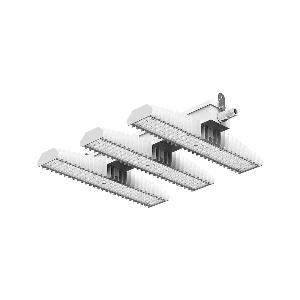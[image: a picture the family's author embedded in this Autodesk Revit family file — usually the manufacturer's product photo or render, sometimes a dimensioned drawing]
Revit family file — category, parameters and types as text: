
# Revit family: 3f_filippi_-_3f_lem_ho_ampio_3f_filippi_-_58973_-_3f_lem_3_ho_led_210_dali_cr_ampio
name_source: partatom
category: Lighting Fixtures
units: mm (PartAtom-declared; Revit-internal decimal feet)

## family parameters
Cut with Voids When Loaded = No
Host = Face
Light Source = No
Part Type = Normal
Room Calculation Point = No
Round Connector Dimension = Use Diameter
Shared = No

## types (1)
- 3F Filippi - 3F LEM HO Ampio (1 x LED, 33909 lm, 207 W, 4000 K)
    Apparent Load = 207 VA
    Approval mark = CE
    CIE Flux Codes = 60 92 99 100 100
    Color Rendering = 80
    Color Temperature = 4000 K
    Control Gear = Electronic transformer
    Default Elevation = 1800 mm
    Description = Industrial luminaire with high light output and high luminous efficiency designed with the most innovative technologies for environments with temperature up to 55°C.

ILLUMINOTECHNICAL
Luminous efficiency 100% (DLOR 100%, ULOR 0%).
Initial luminous flux of the luminaire 33909 lm.
Direct symmetric wide distribution: the illuminated area has a rectangular shape.
Installation Interdistance Transv.D = 1.58 x hu - Long.D = 1.45 x hu.
Tabular UGR (CIE 117 - 4H-8H; S=0.25H; 70/50/20): RUG 24.2 - 25.2.
Beam angle: 93° - 99°.
Luminous efficacy 164 lm/W.
Lifetime (L93/B10): 30000 h. (tq+25°C)
Lifetime (L90/B10): 50000 h. (tq+25°C)
Lifetime (L85/B10): 80000 h. (tq+25°C)
Lifetime (L80/B10): 100000 h. (tq+25°C)
Lifetime (L85/B10): 50000 h. (tq+55°C)
Sudden decreased luminous flux after 50000 hours: 0% (C0).
Photobiological safety in compliance with IEC/TR 62778: RG0 risk exempt, (IEC 62471).
In compliance with IEC/EN 62722-2-1 - IEC/EN 62717 standards.

SOURCE
3 Mid-Power linear LED modules 70W/840.
Energy efficiency class (UE 2019/2020 - UE 2019/2015): C.
CIE 13.3 Colour rendering index: CRI >80 (R9 <50%).
IES TM-30 Fidelity Index: Rf = 84 Rg = 95.
CCT nominal colour temperature 4000 K.
Colour initial tolerance (MacAdam): SDCM 3.

MECHANICAL
Passive modular heatsinks in die-casted aluminium, painted in white colour.
To optimize the thermal management of the LED module, the heatsinks are oversized and provided with self-cleaning of cooling fins.
Wiring body in aluminium and galvanised steel anchored solidly to the sinks and thermally separated.
3F Lens lenses with high luminous efficiency, transparent methacrylate (PMMA), fixed to the LED modules.
Fixing brackets in stainless steel.
Luminaire with limited surface temperature. - D - (EN 60598-2-24)
Dimensions: 657x542 mm, height 129 mm. Weight 13.725 kg.
IP65 protection degree.
Mechanical strength to impacts IK06 (1 joule).
Glow-wire test resistance 650°C.

ELECTRICAL
Halogen Free DALI-2 DATI (Parts 251, 252, 253), PUSH-DIM, electronic wiring 230V-50/60Hz, power factor 0.97 at full load, THD <25%, constant output current, class I, 2 driver, 2 DALI addresses.
Power of the luminaire 207 W.
ENEC - CE.
SAFE FLICKER: PstLM=<1 and SVM=<0.4 (IEC TR 61547-1 and IEC TR 63158), to ensure a more comfortable and safe light.
Luminaire compliant with EN 60598-2-22 for power supply from a centralised emergency system CPSS (Central Power Supply System), not incorporated in the luminaire - high risk areas excluded. The default power and flux are 100% in AC and 15% in DC.
Ambient temperature from -30°C to +55°C.
Temperature class T6 max 85°C.
Quick connection via M25 5P connector with 9-13 mm tightening range.
Power unit positioned on a separate compartment by the LED module to ensure optimum temperatures of cabling components, to be inspectable and maintainable.
Relative humidity UR: <85%.

INSTALLATION
Ceiling / Suspended / Wall.
All accessories dedicated to this product are available on the Catalog and on our website www.3F-Filippi.com.

APPLICATIONS
In commercial environments, exhibition and industrial areas, stores, open areas.
Environments in which it is necessary a total protection against falling fragments (eg environments with foodstuffs or machines with moving parts or with extreme temperature changes), use luminaires with polycarbonate lenses.

LIGHT MANAGEMENT
Recommended minimum setting: 10%.
The luminaire, equipped with (DALI-2 DATI) driver, can be controlled manually with 3F Easy Dim technology or automatically/manually with wired or wireless DALI/D2D control systems.
The D2D driver guarantees interoperability with other devices with the same certification by making the following information available:
Device Data (Part 251), Energy Report (Part 252), Diagnosis & Maintenance (Part 253).
In electrical systems without a regulation system (manual or automatic) and DALI bus, a suitable jumper must be made on the DA-DA terminals of the appliance.

WARNING
Fixture not suitable for cold stores with an ambient temperature <0°C and/or relative humidity >85%.
Luminaire designed for disposal/recycling at end-of-life.
Replaceable (LED only) light source by a professional. Replaceable control gear by a professional.
    Height = 129 mm
    Lamp = 1 x LED
    Lamp Light Flux = 33909 lm
    Lamp Power = 207 W
    Lamp count = 1
    Length = 657 mm
    Lifetime = 50000 h
    Luminous efficacy = 164 lm/W
    Manufacturer = 3F Filippi
    ModVariant = No
    Model = 3F Filippi - 58973 - 3F LEM 3 HO LED 210 DALI CR AMPIO
    Mounting Place = Ceiling
    Mounting Type = Pendant
    Number of Poles = 1
    OnlyDefault = Yes
    Power Factor = 1
    Product Name = 3F Filippi - 3F LEM HO Ampio
    Product group = pendant luminaire
    ProductGroupID = 9
    Protection Class = Protection class I
    Protection Degree = IP 65
    RLX_Detail_Level = 1
    RLX_Emergency_Light_Flux = 0 lm
    RLX_Emergency_Type = 0
    RLX_Emergency_Type_DB = No
    RlxData = <blob elided: 103069 chars, md5=16b3fab2>
    Socket = socket
    Standby Power = 0 W
    System Light Flux = 33909 lm
    System Power = 207 W
    Type Comments = Product without accessories
    Type Image = 3f_filippi_-_lem_3.jpg
    URL = http://relux.com
    VarID = ---
    Voltage = 0 V
    Weight = 0.00 kg
    Width = 542 mm

## geometry (parser evidence)
native form markers: Blend x4, Sweep x11
no freeform markers — native parametric forms only
